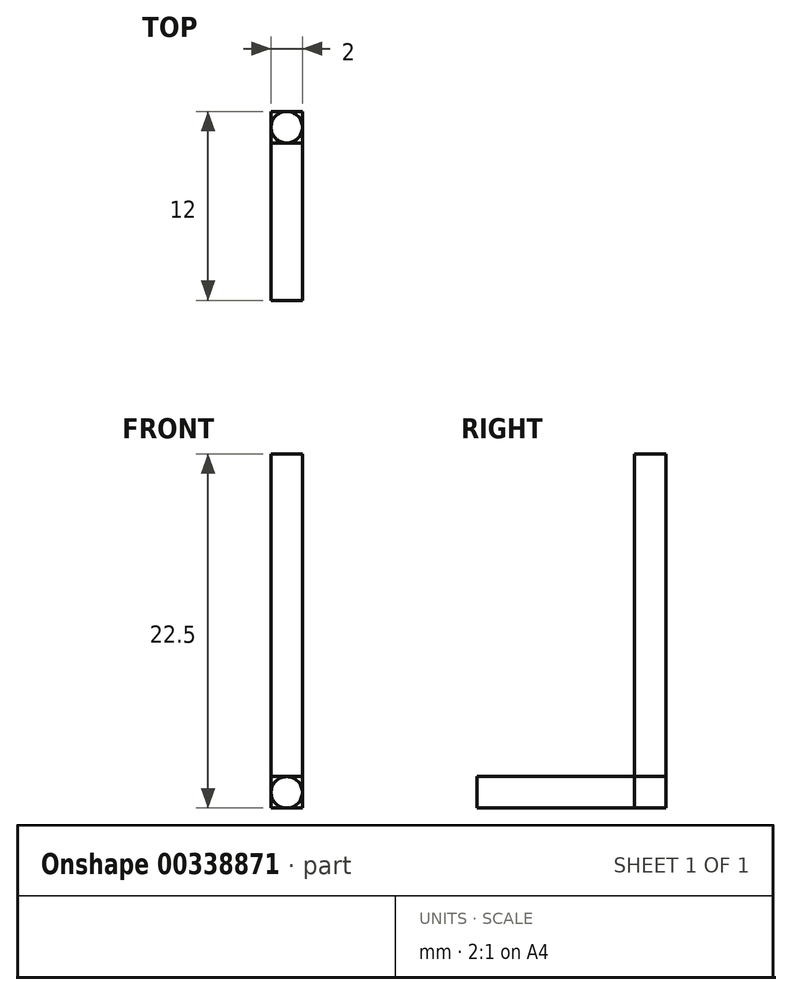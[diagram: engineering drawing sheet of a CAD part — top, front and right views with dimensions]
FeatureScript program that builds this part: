
annotation { "Feature Type Name" : "Feature", "Feature Type Description" : "" }
export const myFeature = defineFeature(function(context is Context, id is Id, definition is map)
    precondition{}
    {
        {
            var Q0;
            Q0=qCreatedBy(makeId("Right.planeOp"),FACE);
            var sketch = newSketch(context, id + "F0", { "sketchPlane" : qUnion([Q0])});
            skLineSegment(sketch, "E0", {"start": v(0, 0) * mm, "end": v(10, 0) * mm});
            skLineSegment(sketch, "E1", {"start": v(10, 0) * mm, "end": v(10, 20.5) * mm});
            skLineSegment(sketch, "E2", {"start": v(10, 20.5) * mm, "end": v(12, 20.5) * mm});
            skLineSegment(sketch, "E3", {"start": v(12, 20.5) * mm, "end": v(12, -2) * mm});
            skLineSegment(sketch, "E4", {"start": v(12, -2) * mm, "end": v(0, -2) * mm});
            skLineSegment(sketch, "E5", {"start": v(0, -2) * mm, "end": v(0, 0) * mm});
            skSolve(sketch);
        }
        {
            var Q0;
            Q0 = qSketchRegion(id + "F0", true);
            extrude(context, id + "F1", {"entities" : qUnion([Q0]), "depth" : 2 * mm});
        }
        {
            var Q0;
            Q0=makeQuery(id+"F1.opExtrude","SWEPT_FACE",FACE,{"disambiguationData":[OSD([sQuery(id+"F0.wireOp",EDGE,"E2")])]});
            var sketch = newSketch(context, id + "F2", { "sketchPlane" : qUnion([Q0])});
            skCircle(sketch, "E6", {"center": v(1, 11) * mm, "radius": 1 * mm});
            skSolve(sketch);
        }
        {
            var Q0;
            {var subQ0=sQuery(id+"F2.wireOp",EDGE,"E6");var subQ1=sQuery(id+"F0.wireOp",EDGE,"E2");var subQ2=makeQuery(id+"F1.opExtrude","CAP_EDGE",EDGE,{"disambiguationData":[OSD([subQ1])],"isStart":true});var subQ3=makeQuery(id+"F2.imprint","INTERSECT",VERTEX,{"derivedFrom":[subQ2,subQ0]});Q0=makeQuery(id+"F2.imprint","IMPRINT",FACE,{"disambiguationData":[TD([[makeQuery(id+"F2.imprint","IMPRINT",EDGE,{"disambiguationData":[TD([[subQ3,-1.0]])],"derivedFrom":subQ0}),-1.0]])]});}
            var Q1;
            {var subQ0=sQuery(id+"F2.wireOp",EDGE,"E6");var subQ1=sQuery(id+"F0.wireOp",EDGE,"E2");var subQ2=makeQuery(id+"F1.opExtrude","CAP_EDGE",EDGE,{"disambiguationData":[OSD([subQ1])],"isStart":false});var subQ3=makeQuery(id+"F2.imprint","INTERSECT",VERTEX,{"derivedFrom":[subQ2,subQ0]});Q1=makeQuery(id+"F2.imprint","IMPRINT",FACE,{"disambiguationData":[TD([[makeQuery(id+"F2.imprint","IMPRINT",EDGE,{"disambiguationData":[TD([[subQ3,1.0]])],"derivedFrom":subQ0}),-1.0]])]});}
            var Q2;
            {var subQ0=sQuery(id+"F2.wireOp",EDGE,"E6");var subQ1=sQuery(id+"F0.wireOp",EDGE,"E2");var subQ4=makeQuery(id+"F1.opExtrude","CAP_EDGE",EDGE,{"disambiguationData":[OSD([subQ1])],"isStart":false});var subQ5=makeQuery(id+"F2.imprint","INTERSECT",VERTEX,{"derivedFrom":[subQ4,subQ0]});Q2=makeQuery(id+"F2.imprint","IMPRINT",FACE,{"disambiguationData":[TD([[makeQuery(id+"F2.imprint","IMPRINT",EDGE,{"disambiguationData":[TD([[subQ5,-1.0]])],"derivedFrom":subQ0}),-1.0]])]});}
            var Q3;
            {var subQ0=sQuery(id+"F2.wireOp",EDGE,"E6");var subQ1=sQuery(id+"F0.wireOp",EDGE,"E2");var subQ4=makeQuery(id+"F1.opExtrude","CAP_EDGE",EDGE,{"disambiguationData":[OSD([subQ1])],"isStart":true});var subQ5=makeQuery(id+"F2.imprint","INTERSECT",VERTEX,{"derivedFrom":[subQ4,subQ0]});Q3=makeQuery(id+"F2.imprint","IMPRINT",FACE,{"disambiguationData":[TD([[makeQuery(id+"F2.imprint","IMPRINT",EDGE,{"disambiguationData":[TD([[subQ5,1.0]])],"derivedFrom":subQ0}),-1.0]])]});}
            extrude(context, id + "F3", {"entities" : qUnion([Q0, Q1, Q2, Q3]), "operationType" : NewBodyOperationType.REMOVE, "oppositeDirection" : true, "depth" : 20.5 * mm});
        }
        {
            var Q0;
            Q0=makeQuery(id+"F1.opExtrude","SWEPT_FACE",FACE,{"disambiguationData":[OSD([sQuery(id+"F0.wireOp",EDGE,"E5")])]});
            var sketch = newSketch(context, id + "F4", { "sketchPlane" : qUnion([Q0])});
            skCircle(sketch, "E7", {"center": v(1, -1) * mm, "radius": 1 * mm});
            skSolve(sketch);
        }
        {
            var Q0;
            {var subQ0=sQuery(id+"F4.wireOp",EDGE,"E7");var subQ1=sQuery(id+"F0.wireOp",EDGE,"E5");var subQ4=makeQuery(id+"F1.opExtrude","CAP_EDGE",EDGE,{"disambiguationData":[OSD([subQ1])],"isStart":true});var subQ5=makeQuery(id+"F4.imprint","INTERSECT",VERTEX,{"derivedFrom":[subQ4,subQ0]});Q0=makeQuery(id+"F4.imprint","IMPRINT",FACE,{"disambiguationData":[TD([[makeQuery(id+"F4.imprint","IMPRINT",EDGE,{"disambiguationData":[TD([[subQ5,1.0]])],"derivedFrom":subQ0}),-1.0]])]});}
            var Q1;
            {var subQ0=sQuery(id+"F4.wireOp",EDGE,"E7");var subQ1=sQuery(id+"F0.wireOp",EDGE,"E5");var subQ4=makeQuery(id+"F1.opExtrude","CAP_EDGE",EDGE,{"disambiguationData":[OSD([subQ1])],"isStart":false});var subQ5=makeQuery(id+"F4.imprint","INTERSECT",VERTEX,{"derivedFrom":[subQ4,subQ0]});Q1=makeQuery(id+"F4.imprint","IMPRINT",FACE,{"disambiguationData":[TD([[makeQuery(id+"F4.imprint","IMPRINT",EDGE,{"disambiguationData":[TD([[subQ5,-1.0]])],"derivedFrom":subQ0}),-1.0]])]});}
            var Q2;
            {var subQ0=sQuery(id+"F4.wireOp",EDGE,"E7");var subQ1=sQuery(id+"F0.wireOp",EDGE,"E5");var subQ2=makeQuery(id+"F1.opExtrude","CAP_EDGE",EDGE,{"disambiguationData":[OSD([subQ1])],"isStart":false});var subQ3=makeQuery(id+"F4.imprint","INTERSECT",VERTEX,{"derivedFrom":[subQ2,subQ0]});Q2=makeQuery(id+"F4.imprint","IMPRINT",FACE,{"disambiguationData":[TD([[makeQuery(id+"F4.imprint","IMPRINT",EDGE,{"disambiguationData":[TD([[subQ3,1.0]])],"derivedFrom":subQ0}),-1.0]])]});}
            var Q3;
            {var subQ0=sQuery(id+"F4.wireOp",EDGE,"E7");var subQ1=sQuery(id+"F0.wireOp",EDGE,"E5");var subQ2=makeQuery(id+"F1.opExtrude","CAP_EDGE",EDGE,{"disambiguationData":[OSD([subQ1])],"isStart":true});var subQ3=makeQuery(id+"F4.imprint","INTERSECT",VERTEX,{"derivedFrom":[subQ2,subQ0]});Q3=makeQuery(id+"F4.imprint","IMPRINT",FACE,{"disambiguationData":[TD([[makeQuery(id+"F4.imprint","IMPRINT",EDGE,{"disambiguationData":[TD([[subQ3,-1.0]])],"derivedFrom":subQ0}),-1.0]])]});}
            extrude(context, id + "F5", {"entities" : qUnion([Q0, Q1, Q2, Q3]), "operationType" : NewBodyOperationType.REMOVE, "oppositeDirection" : true, "depth" : 10 * mm});
        }
    });
